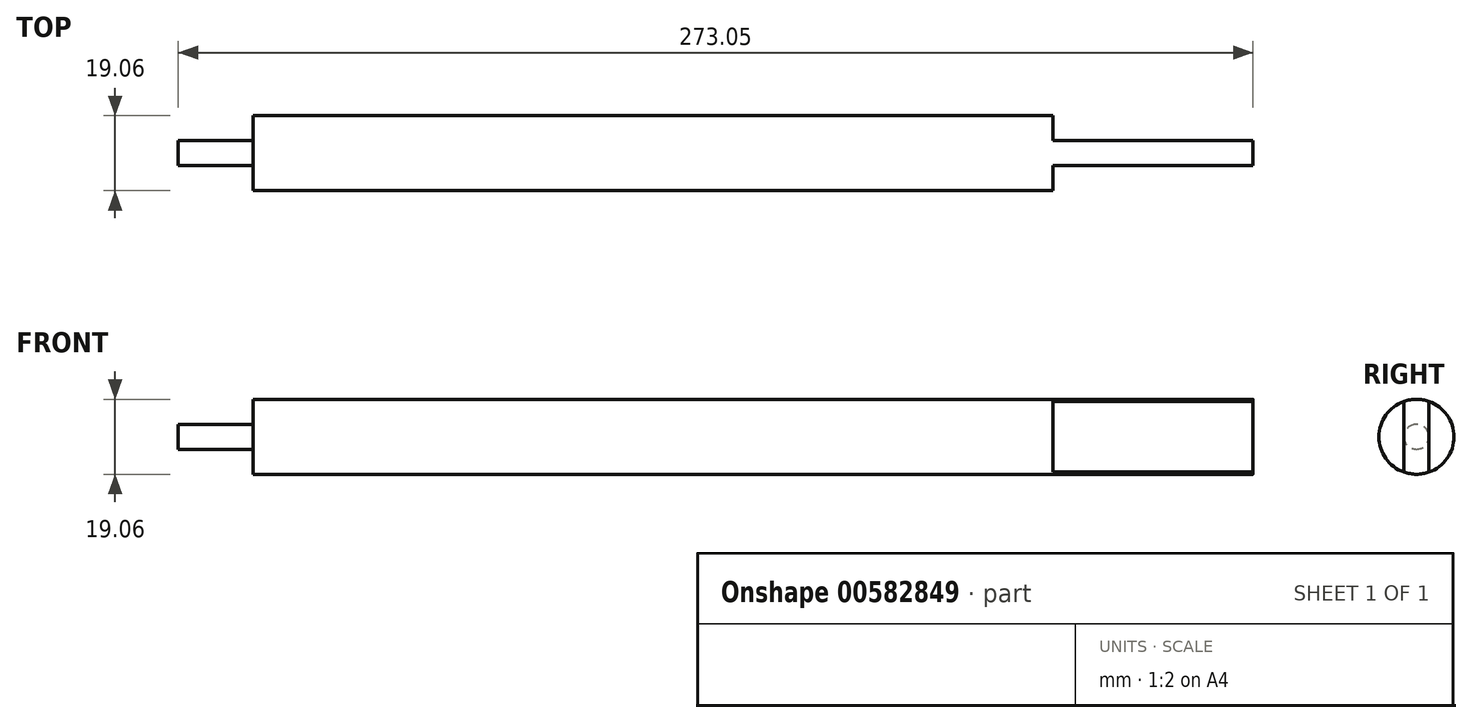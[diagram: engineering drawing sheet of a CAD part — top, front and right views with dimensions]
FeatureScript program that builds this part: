
annotation { "Feature Type Name" : "Feature", "Feature Type Description" : "" }
export const myFeature = defineFeature(function(context is Context, id is Id, definition is map)
    precondition{}
    {
        {
            var Q0;
            Q0=qCreatedBy(makeId("Top.planeOp"),FACE);
            var sketch = newSketch(context, id + "F0", { "sketchPlane" : qUnion([Q0])});
            skLineSegment(sketch, "E0.bottom", {"start": v(-127, -9.53) * mm, "end": v(127, -9.53) * mm});
            skLineSegment(sketch, "E0.top", {"start": v(-127, 9.53) * mm, "end": v(127, 9.53) * mm});
            skLineSegment(sketch, "E0.left", {"start": v(-127, -9.53) * mm, "end": v(-127, 9.53) * mm});
            skLineSegment(sketch, "E0.right", {"start": v(127, -9.53) * mm, "end": v(127, 9.53) * mm});
            skPoint(sketch, "E0.middle", {"position": v(0, 0) * mm});
            skLineSegment(sketch, "E1.bottom", {"start": v(-127, 3.18) * mm, "end": v(-146.05, 3.18) * mm});
            skLineSegment(sketch, "E1.top", {"start": v(-127, -3.18) * mm, "end": v(-146.05, -3.18) * mm});
            skLineSegment(sketch, "E1.left", {"start": v(-127, 3.18) * mm, "end": v(-127, -3.17) * mm});
            skLineSegment(sketch, "E1.right", {"start": v(-146.05, 3.18) * mm, "end": v(-146.05, -3.17) * mm});
            skLineSegment(sketch, "E2", {"start": v(127, 0) * mm, "end": v(-146.05, 0) * mm});
            skSolve(sketch);
        }
        {
            var Q0;
            {var subQ1=sQuery(id+"F0.wireOp",EDGE,"E0.top");Q0=makeQuery(id+"F0.imprint","IMPRINT",FACE,{"disambiguationData":[TD([[makeQuery(id+"F0.imprint","IMPRINT",EDGE,{"derivedFrom":subQ1}),-1.0]])]});}
            var Q1;
            {var subQ6=sQuery(id+"F0.wireOp",EDGE,"E0.bottom");Q1=makeQuery(id+"F0.imprint","IMPRINT",FACE,{"disambiguationData":[TD([[makeQuery(id+"F0.imprint","IMPRINT",EDGE,{"derivedFrom":subQ6}),1.0]])]});}
            var Q2;
            {var subQ0=sQuery(id+"F0.wireOp",EDGE,"E1.bottom");Q2=makeQuery(id+"F0.imprint","IMPRINT",FACE,{"disambiguationData":[TD([[makeQuery(id+"F0.imprint","IMPRINT",EDGE,{"derivedFrom":subQ0}),1.0]])]});}
            var Q3;
            {var subQ0=sQuery(id+"F0.wireOp",EDGE,"E1.top");Q3=makeQuery(id+"F0.imprint","IMPRINT",FACE,{"disambiguationData":[TD([[makeQuery(id+"F0.imprint","IMPRINT",EDGE,{"derivedFrom":subQ0}),-1.0]])]});}
            extrude(context, id + "F1", {"entities" : qUnion([Q0, Q1, Q2, Q3]), "endBound" : BoundingType.SYMMETRIC, "depth" : 19.05 * mm, "offsetDistance" : 25.4 * mm});
        }
        {
            var Q0;
            Q0=qCreatedBy(makeId("Top.planeOp"),FACE);
            var sketch = newSketch(context, id + "F2", { "sketchPlane" : qUnion([Q0])});
            skLineSegment(sketch, "E3.bottom", {"start": v(127, 9.53) * mm, "end": v(76.2, 9.53) * mm});
            skLineSegment(sketch, "E3.top", {"start": v(127, -9.53) * mm, "end": v(76.2, -9.53) * mm});
            skLineSegment(sketch, "E3.left", {"start": v(127, 9.53) * mm, "end": v(127, -9.53) * mm});
            skLineSegment(sketch, "E3.right", {"start": v(76.2, 9.52) * mm, "end": v(76.2, -9.53) * mm});
            skLineSegment(sketch, "E4.bottom", {"start": v(127, 3.18) * mm, "end": v(76.2, 3.17) * mm});
            skLineSegment(sketch, "E4.top", {"start": v(127, -3.17) * mm, "end": v(76.2, -3.18) * mm});
            skLineSegment(sketch, "E4.left", {"start": v(127, 3.18) * mm, "end": v(127, -3.17) * mm});
            skLineSegment(sketch, "E4.right", {"start": v(76.2, 3.17) * mm, "end": v(76.2, -3.18) * mm});
            skSolve(sketch);
        }
        {
            var Q0;
            {var subQ0=sQuery(id+"F2.wireOp",EDGE,"E3.bottom");Q0=makeQuery(id+"F2.imprint","IMPRINT",FACE,{"disambiguationData":[TD([[makeQuery(id+"F2.imprint","IMPRINT",EDGE,{"derivedFrom":subQ0}),1.0]])]});}
            var Q1;
            {var subQ0=sQuery(id+"F2.wireOp",EDGE,"E3.top");Q1=makeQuery(id+"F2.imprint","IMPRINT",FACE,{"disambiguationData":[TD([[makeQuery(id+"F2.imprint","IMPRINT",EDGE,{"derivedFrom":subQ0}),-1.0]])]});}
            extrude(context, id + "F3", {"entities" : qUnion([Q0, Q1]), "operationType" : NewBodyOperationType.REMOVE, "endBound" : BoundingType.SYMMETRIC, "oppositeDirection" : true, "depth" : 25.4 * mm, "offsetDistance" : 25.4 * mm});
        }
        {
            var Q0;
            Q0=makeQuery(id+"F1.opExtrude","SWEPT_FACE",FACE,{"disambiguationData":[OSD([sQuery(id+"F0.wireOp",EDGE,"E0.right")])]});
            var sketch = newSketch(context, id + "F4", { "sketchPlane" : qUnion([Q0])});
            skCircle(sketch, "E5", {"center": v(0, 0) * mm, "radius": 9.52 * mm});
            skLineSegment(sketch, "E6.bottom", {"start": v(-9.53, -9.53) * mm, "end": v(9.52, -9.53) * mm});
            skLineSegment(sketch, "E6.top", {"start": v(-9.53, 9.53) * mm, "end": v(9.53, 9.53) * mm});
            skLineSegment(sketch, "E6.left", {"start": v(-9.53, -9.53) * mm, "end": v(-9.52, 9.52) * mm});
            skLineSegment(sketch, "E6.right", {"start": v(9.53, -9.52) * mm, "end": v(9.53, 9.53) * mm});
            skSolve(sketch);
        }
        {
            var Q0;
            {var subQ0=sQuery(id+"F4.wireOp",EDGE,"E6.left");var subQ5=sQuery(id+"F4.wireOp",EDGE,"E6.top");var subQ7=makeQuery(id+"F4.imprint","INTERSECT",VERTEX,{"derivedFrom":[subQ5,subQ0]});Q0=makeQuery(id+"F4.imprint","IMPRINT",FACE,{"disambiguationData":[TD([[makeQuery(id+"F4.imprint","IMPRINT",EDGE,{"disambiguationData":[TD([[subQ7,1.0]])],"derivedFrom":subQ0}),-1.0]])]});}
            var Q1;
            {var subQ0=sQuery(id+"F4.wireOp",EDGE,"E6.left");var subQ5=sQuery(id+"F4.wireOp",EDGE,"E6.bottom");var subQ7=makeQuery(id+"F4.imprint","INTERSECT",VERTEX,{"derivedFrom":[subQ5,subQ0]});Q1=makeQuery(id+"F4.imprint","IMPRINT",FACE,{"disambiguationData":[TD([[makeQuery(id+"F4.imprint","IMPRINT",EDGE,{"disambiguationData":[TD([[subQ7,-1.0]])],"derivedFrom":subQ0}),-1.0]])]});}
            var Q2;
            {var subQ0=sQuery(id+"F4.wireOp",EDGE,"E6.right");var subQ5=sQuery(id+"F4.wireOp",EDGE,"E6.bottom");var subQ7=makeQuery(id+"F4.imprint","INTERSECT",VERTEX,{"derivedFrom":[subQ5,subQ0]});Q2=makeQuery(id+"F4.imprint","IMPRINT",FACE,{"disambiguationData":[TD([[makeQuery(id+"F4.imprint","IMPRINT",EDGE,{"disambiguationData":[TD([[subQ7,-1.0]])],"derivedFrom":subQ0}),1.0]])]});}
            var Q3;
            {var subQ0=sQuery(id+"F4.wireOp",EDGE,"E6.right");var subQ5=sQuery(id+"F4.wireOp",EDGE,"E6.top");var subQ7=makeQuery(id+"F4.imprint","INTERSECT",VERTEX,{"derivedFrom":[subQ5,subQ0]});Q3=makeQuery(id+"F4.imprint","IMPRINT",FACE,{"disambiguationData":[TD([[makeQuery(id+"F4.imprint","IMPRINT",EDGE,{"disambiguationData":[TD([[subQ7,1.0]])],"derivedFrom":subQ0}),1.0]])]});}
            var Q4;
            {var subQ0=sQuery(id+"F4.wireOp",EDGE,"E6.top");var subQ1=sQuery(id+"F4.wireOp",EDGE,"E5");var subQ2=makeQuery(id+"F4.imprint","INTERSECT",VERTEX,{"derivedFrom":[subQ1,subQ0]});Q4=makeQuery(id+"F4.imprint","IMPRINT",FACE,{"disambiguationData":[TD([[makeQuery(id+"F4.imprint","IMPRINT",EDGE,{"disambiguationData":[TD([[subQ2,-1.0]])],"derivedFrom":subQ1}),-1.0]])]});}
            var Q5;
            {var subQ0=sQuery(id+"F4.wireOp",EDGE,"E6.top");var subQ1=sQuery(id+"F4.wireOp",EDGE,"E5");var subQ2=makeQuery(id+"F4.imprint","INTERSECT",VERTEX,{"derivedFrom":[subQ1,subQ0]});Q5=makeQuery(id+"F4.imprint","IMPRINT",FACE,{"disambiguationData":[TD([[makeQuery(id+"F4.imprint","IMPRINT",EDGE,{"disambiguationData":[TD([[subQ2,1.0]])],"derivedFrom":subQ1}),-1.0]])]});}
            var Q6;
            {var subQ0=sQuery(id+"F4.wireOp",EDGE,"E6.bottom");var subQ1=sQuery(id+"F4.wireOp",EDGE,"E5");var subQ2=makeQuery(id+"F4.imprint","INTERSECT",VERTEX,{"derivedFrom":[subQ1,subQ0]});Q6=makeQuery(id+"F4.imprint","IMPRINT",FACE,{"disambiguationData":[TD([[makeQuery(id+"F4.imprint","IMPRINT",EDGE,{"disambiguationData":[TD([[subQ2,-1.0]])],"derivedFrom":subQ1}),-1.0]])]});}
            var Q7;
            {var subQ0=sQuery(id+"F4.wireOp",EDGE,"E6.bottom");var subQ1=sQuery(id+"F4.wireOp",EDGE,"E5");var subQ2=makeQuery(id+"F4.imprint","INTERSECT",VERTEX,{"derivedFrom":[subQ1,subQ0]});Q7=makeQuery(id+"F4.imprint","IMPRINT",FACE,{"disambiguationData":[TD([[makeQuery(id+"F4.imprint","IMPRINT",EDGE,{"disambiguationData":[TD([[subQ2,1.0]])],"derivedFrom":subQ1}),-1.0]])]});}
            extrude(context, id + "F5", {"entities" : qUnion([Q0, Q1, Q2, Q3, Q4, Q5, Q6, Q7]), "operationType" : NewBodyOperationType.REMOVE, "endBound" : BoundingType.THROUGH_ALL, "oppositeDirection" : true, "depth" : 25.4 * mm, "offsetDistance" : 25.4 * mm});
        }
        {
            var Q0;
            Q0=makeQuery(id+"F1.opExtrude","SWEPT_FACE",FACE,{"disambiguationData":[OSD([sQuery(id+"F0.wireOp",EDGE,"E1.right")])]});
            var sketch = newSketch(context, id + "F6", { "sketchPlane" : qUnion([Q0])});
            skCircle(sketch, "E7", {"center": v(0, 0) * mm, "radius": 3.17 * mm});
            skLineSegment(sketch, "E8.bottom", {"start": v(-3.18, -9.52) * mm, "end": v(3.18, -9.52) * mm});
            skLineSegment(sketch, "E8.top", {"start": v(-3.18, 9.52) * mm, "end": v(3.18, 9.52) * mm});
            skLineSegment(sketch, "E8.left", {"start": v(-3.18, -9.52) * mm, "end": v(-3.18, 9.52) * mm});
            skLineSegment(sketch, "E8.right", {"start": v(3.18, -9.52) * mm, "end": v(3.18, 9.52) * mm});
            skSolve(sketch);
        }
        {
            var Q0;
            {var subQ16=sQuery(id+"F6.wireOp",EDGE,"E7");var subQ18=sQuery(id+"F6.wireOp",EDGE,"E8.left");var subQ21=makeQuery(id+"F6.imprint","INTERSECT",VERTEX,{"derivedFrom":[subQ16,subQ18]});Q0=makeQuery(id+"F6.imprint","IMPRINT",FACE,{"disambiguationData":[TD([[makeQuery(id+"F6.imprint","IMPRINT",EDGE,{"disambiguationData":[TD([[subQ21,-1.0]])],"derivedFrom":subQ16}),-1.0]])]});}
            extrude(context, id + "F7", {"entities" : qUnion([Q0]), "operationType" : NewBodyOperationType.REMOVE, "oppositeDirection" : true, "depth" : 19.05 * mm, "offsetDistance" : 25.4 * mm});
        }
        {
            var Q0;
            {var subQ0=sQuery(id+"F6.wireOp",EDGE,"E8.left");var subQ12=sQuery(id+"F6.wireOp",EDGE,"E7");var subQ14=makeQuery(id+"F6.imprint","INTERSECT",VERTEX,{"derivedFrom":[subQ12,subQ0]});Q0=makeQuery(id+"F6.imprint","IMPRINT",FACE,{"disambiguationData":[TD([[makeQuery(id+"F6.imprint","IMPRINT",EDGE,{"disambiguationData":[TD([[subQ14,1.0]])],"derivedFrom":subQ12}),-1.0]])]});}
            extrude(context, id + "F8", {"entities" : qUnion([Q0]), "operationType" : NewBodyOperationType.REMOVE, "oppositeDirection" : true, "depth" : 19.05 * mm, "offsetDistance" : 25.4 * mm});
        }
    });
